# Revit family: BuzziSol
name_source: partatom
category: Lighting Fixtures
revit_build: Autodesk Revit 2018 (Build: 20190510_1515(x64)
units: mm (PartAtom-declared; Revit-internal decimal feet)

## family parameters
Always vertical = Yes
Cut with Voids When Loaded = No
Host = Ceiling
Light Source = No
Part Type = Normal
Room Calculation Point = No
Round Connector Dimension = Use Diameter
Shared = No

## types (6) — shared parameters
Light Source = <By Category>

## per-type parameters (varying)
| type | Canopy Type | Fixture Crossbar Length | Fixture Type | Multilamp | Quintet |
| Solo Globe | Canopy : Solo | 2' - 8 7/16" | Lamp : Globe | No | No |
| Solo Spot | Canopy : Solo | 2' - 8 7/16" | Lamp : Spot | No | No |
| Trio Globe | Canopy : Trio | 2' - 8 7/16" | Lamp : Globe | Yes | No |
| Trio Spot | Canopy : Trio | 2' - 8 7/16" | Lamp : Spot | Yes | No |
| Quintet Globe | Canopy : Quintet | 5' - 2" | Lamp : Globe | Yes | Yes |
| Quintet Spot | Canopy : Quintet | 5' - 2" | Lamp : Spot | Yes | Yes |

## geometry (parser evidence)
native form markers: Sweep x8
no freeform markers — native parametric forms only
